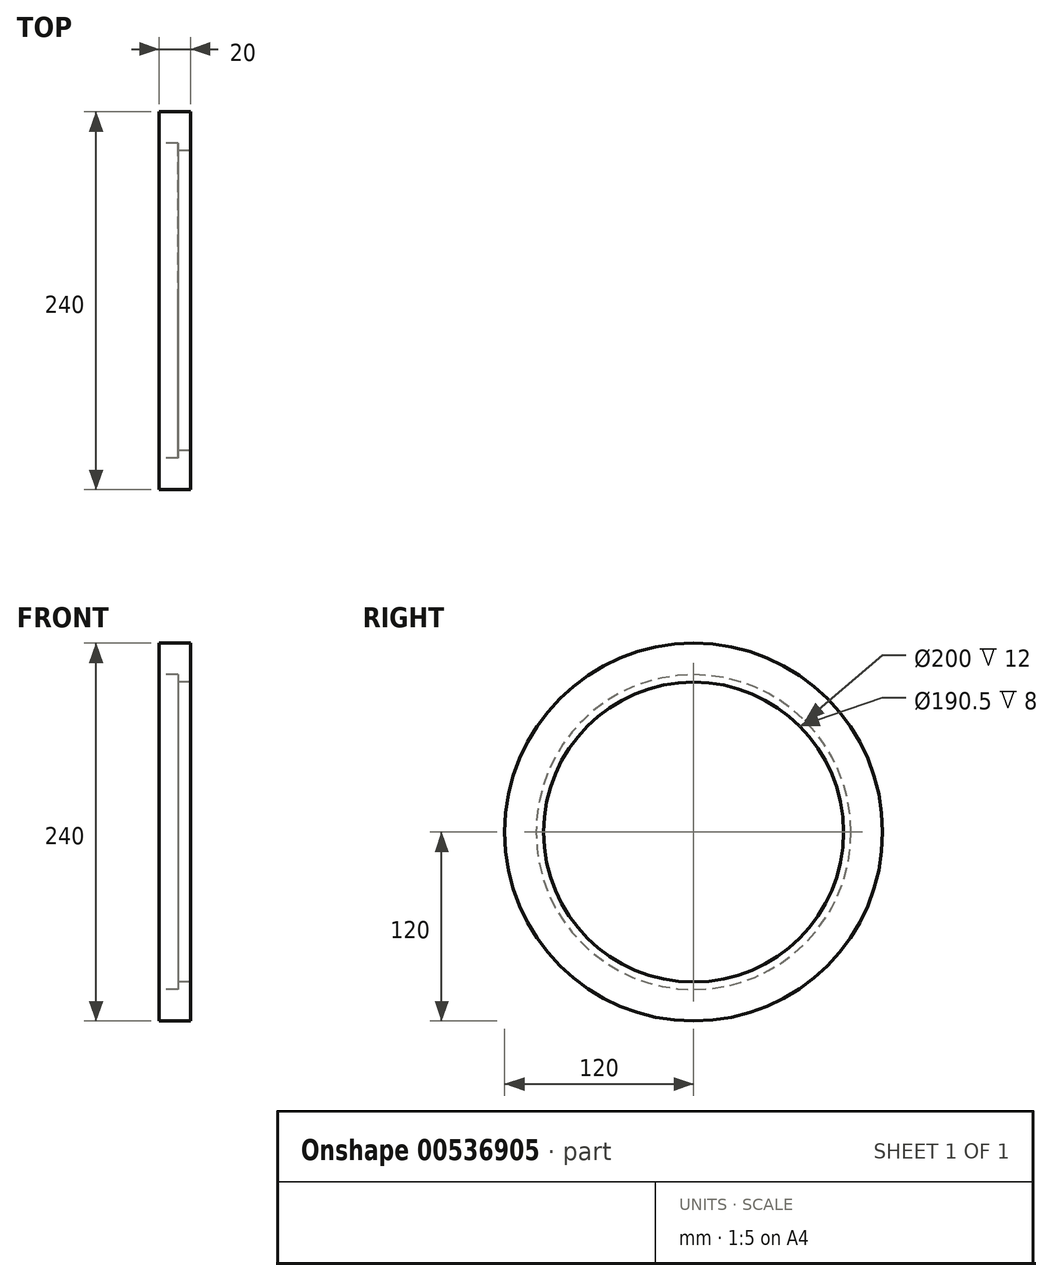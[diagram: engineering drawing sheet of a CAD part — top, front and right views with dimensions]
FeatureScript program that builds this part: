
annotation { "Feature Type Name" : "Feature", "Feature Type Description" : "" }
export const myFeature = defineFeature(function(context is Context, id is Id, definition is map)
    precondition{}
    {
        {
            var Q0;
            Q0=qCreatedBy(makeId("Front.planeOp"),FACE);
            var sketch = newSketch(context, id + "F0", { "sketchPlane" : qUnion([Q0])});
            skLineSegment(sketch, "E0", {"start": v(12, 95.25) * mm, "end": v(12, 100) * mm});
            skLineSegment(sketch, "E1", {"start": v(12, 100) * mm, "end": v(0, 100) * mm});
            skLineSegment(sketch, "E2", {"start": v(0, 100) * mm, "end": v(0, 120) * mm});
            skLineSegment(sketch, "E3", {"start": v(0, 120) * mm, "end": v(20, 120) * mm});
            skLineSegment(sketch, "E4", {"start": v(20, 120) * mm, "end": v(20, 95.25) * mm});
            skLineSegment(sketch, "E5", {"start": v(20, 95.25) * mm, "end": v(12, 95.25) * mm});
            skLineSegment(sketch, "E6", {"start": v(0, 0) * mm, "end": v(20, 0) * mm, "construction": true});
            skLineSegment(sketch, "E7", {"start": v(12, 98.25) * mm, "end": v(12.5, 98.25) * mm});
            skLineSegment(sketch, "E8", {"start": v(12.5, 98.25) * mm, "end": v(12.5, 100) * mm});
            skLineSegment(sketch, "E9", {"start": v(12.5, 100) * mm, "end": v(12, 100) * mm});
            skSolve(sketch);
        }
        {
            var Q0;
            Q0=qSketchRegion(id+"F0",true);
            var Q1;
            Q1=sQuery(id+"F0.wireOp",EDGE,"E6");
            revolve(context, id + "F1", {"entities" : qUnion([Q0]), "axis" : qUnion([Q1]), "revolveType" : RevolveType.FULL});
        }
    });
